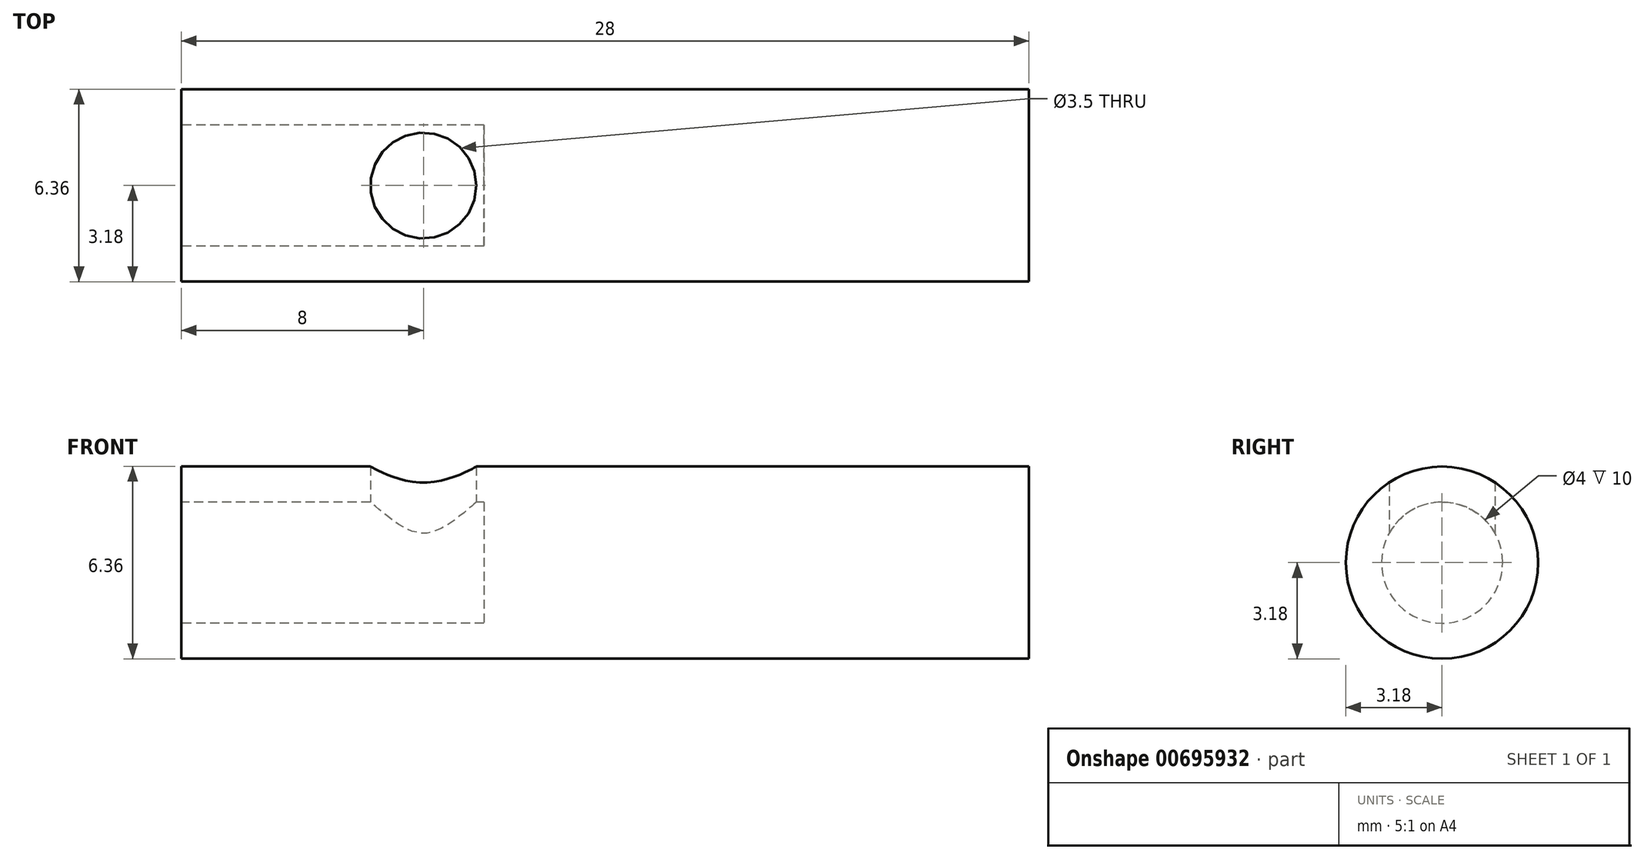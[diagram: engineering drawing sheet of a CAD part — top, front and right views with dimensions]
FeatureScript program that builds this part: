
annotation { "Feature Type Name" : "Feature", "Feature Type Description" : "" }
export const myFeature = defineFeature(function(context is Context, id is Id, definition is map)
    precondition{}
    {
        {
            var Q0;
            Q0=qCreatedBy(makeId("Right.planeOp"),FACE);
            var sketch = newSketch(context, id + "F0", { "sketchPlane" : qUnion([Q0])});
            skCircle(sketch, "E0", {"center": v(0, 0) * mm, "radius": 3.18 * mm});
            skSolve(sketch);
        }
        {
            var Q0;
            Q0 = qSketchRegion(id + "F0", true);
            extrude(context, id + "F1", {"entities" : qUnion([Q0]), "depth" : 28 * mm, "offsetDistance" : 25 * mm});
        }
        {
            var Q0;
            Q0=makeQuery(id+"F1.opExtrude","CAP_FACE",FACE,{"disambiguationData":[OSD([sQuery(id+"F0.wireOp",EDGE,"E0")])],"isStart":true});
            var sketch = newSketch(context, id + "F2", { "sketchPlane" : qUnion([Q0])});
            skCircle(sketch, "E1", {"center": v(0, 0) * mm, "radius": 2 * mm});
            skSolve(sketch);
        }
        {
            var Q0;
            Q0 = qSketchRegion(id + "F2", true);
            extrude(context, id + "F3", {"entities" : qUnion([Q0]), "operationType" : NewBodyOperationType.REMOVE, "oppositeDirection" : true, "depth" : 10 * mm, "offsetDistance" : 25 * mm});
        }
        {
            var Q0;
            Q0=qCreatedBy(makeId("Top.planeOp"),FACE);
            var sketch = newSketch(context, id + "F4", { "sketchPlane" : qUnion([Q0])});
            skLineSegment(sketch, "E2", {"start": v(8, 4) * mm, "end": v(8, -3.92) * mm, "construction": true});
            skCircle(sketch, "E3", {"center": v(8, 0) * mm, "radius": 1.75 * mm});
            skSolve(sketch);
        }
        {
            var Q0;
            Q0 = qSketchRegion(id + "F4", true);
            extrude(context, id + "F5", {"entities" : qUnion([Q0]), "operationType" : NewBodyOperationType.REMOVE, "endBound" : BoundingType.THROUGH_ALL, "depth" : 25 * mm, "offsetDistance" : 25 * mm});
        }
    });
